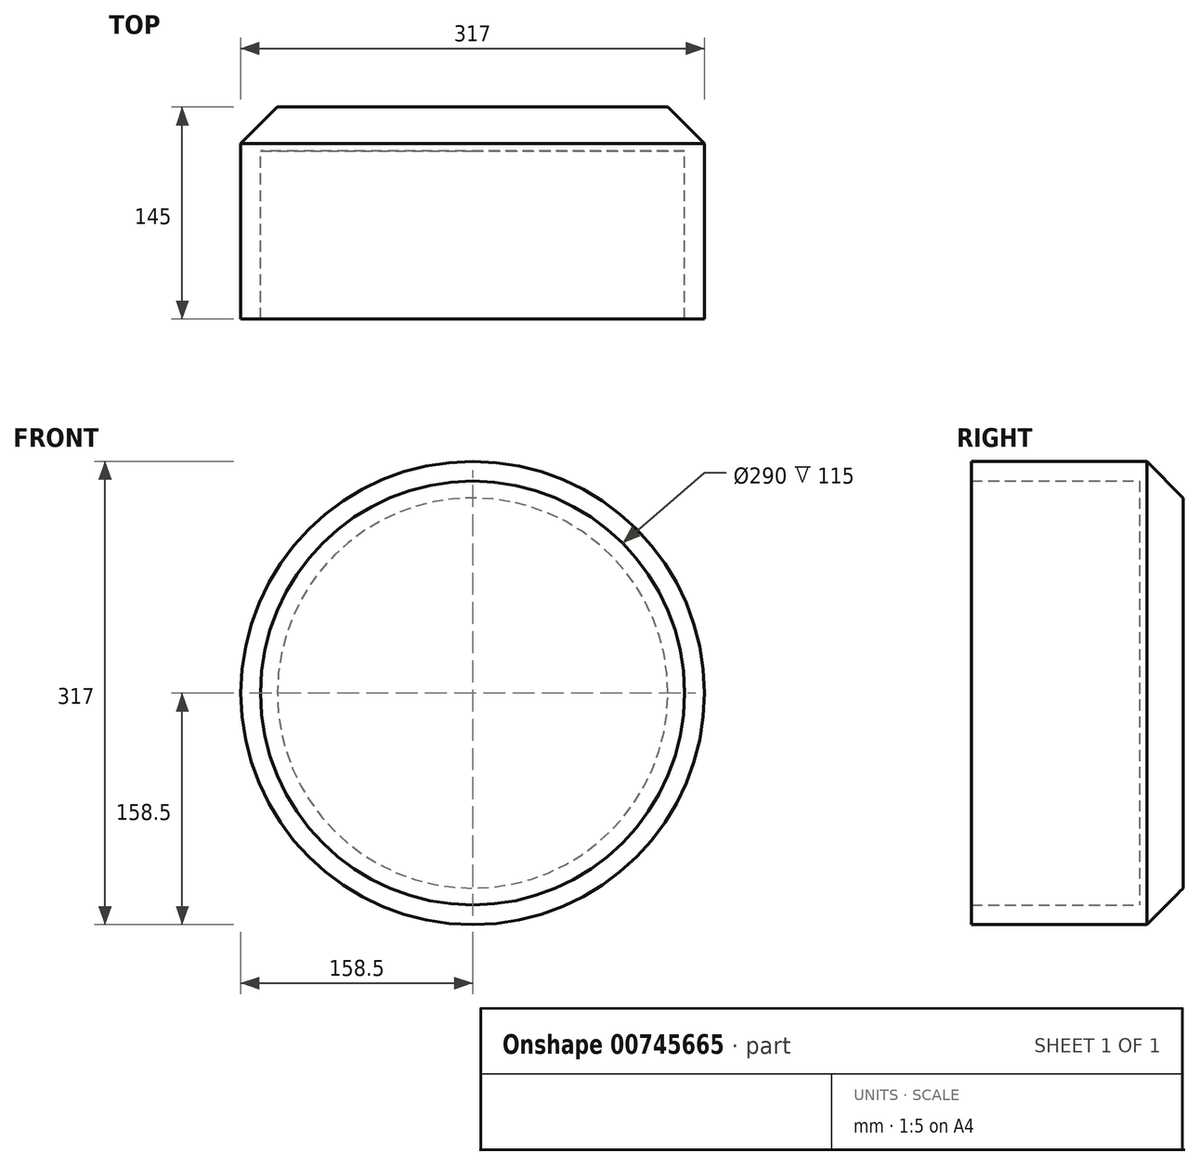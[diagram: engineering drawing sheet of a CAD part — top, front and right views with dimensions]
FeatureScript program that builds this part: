
annotation { "Feature Type Name" : "Feature", "Feature Type Description" : "" }
export const myFeature = defineFeature(function(context is Context, id is Id, definition is map)
    precondition{}
    {
        {
            var Q0;
            Q0=qCreatedBy(makeId("Front.planeOp"),FACE);
            var sketch = newSketch(context, id + "F0", { "sketchPlane" : qUnion([Q0])});
            skCircle(sketch, "E0", {"center": v(0, 0) * mm, "radius": 145 * mm});
            skCircle(sketch, "E1", {"center": v(0, 0) * mm, "radius": 158.5 * mm});
            skSolve(sketch);
        }
        {
            var Q0;
            Q0=makeQuery(id+"F0.imprint","IMPRINT",FACE,{"disambiguationData":[TD([[makeQuery(id+"F0.imprint","IMPRINT",EDGE,{"derivedFrom":sQuery(id+"F0.wireOp",EDGE,"E0")}),-1.0]])]});
            extrude(context, id + "F1", {"entities" : qUnion([Q0]), "depth" : 125 * mm, "offsetDistance" : 25 * mm});
        }
        {
            var Q0;
            Q0=makeQuery(id+"F1.opExtrude","CAP_FACE",FACE,{"disambiguationData":[OSD([sQuery(id+"F0.wireOp",EDGE,"E0"),sQuery(id+"F0.wireOp",EDGE,"E1")])],"isStart":true});
            var sketch = newSketch(context, id + "F2", { "sketchPlane" : qUnion([Q0])});
            skCircle(sketch, "E2.0", {"center": v(0, 0) * mm, "radius": 158.5 * mm});
            skSolve(sketch);
        }
        {
            var Q0;
            Q0 = qSketchRegion(id + "F2", true);
            var Q1;
            Q1=sQuery(id+"F2.wireOp",EDGE,"E2.0");
            extrude(context, id + "F3", {"entities" : qUnion([Q0]), "operationType" : NewBodyOperationType.ADD, "surfaceEntities" : qUnion([Q1]), "oppositeDirection" : true, "depth" : 30 * mm, "offsetDistance" : 25 * mm});
        }
        {
            var Q0;
            Q0=makeQuery(id+"F1.opExtrude","CAP_EDGE",EDGE,{"disambiguationData":[OSD([sQuery(id+"F0.wireOp",EDGE,"E1")])],"isStart":true});
            chamfer(context, id + "F4", {"entities" : qUnion([Q0]), "width" : 25 * mm, "tangentPropagation" : true});
        }
        {
            var Q0;
            Q0=makeQuery(id+"F1.opExtrude","CAP_FACE",FACE,{"disambiguationData":[OSD([sQuery(id+"F0.wireOp",EDGE,"E0"),sQuery(id+"F0.wireOp",EDGE,"E1")])],"isStart":false});
            extrude(context, id + "F5", {"entities" : qUnion([Q0]), "operationType" : NewBodyOperationType.ADD, "depth" : 20 * mm, "offsetDistance" : 25 * mm});
        }
    });
